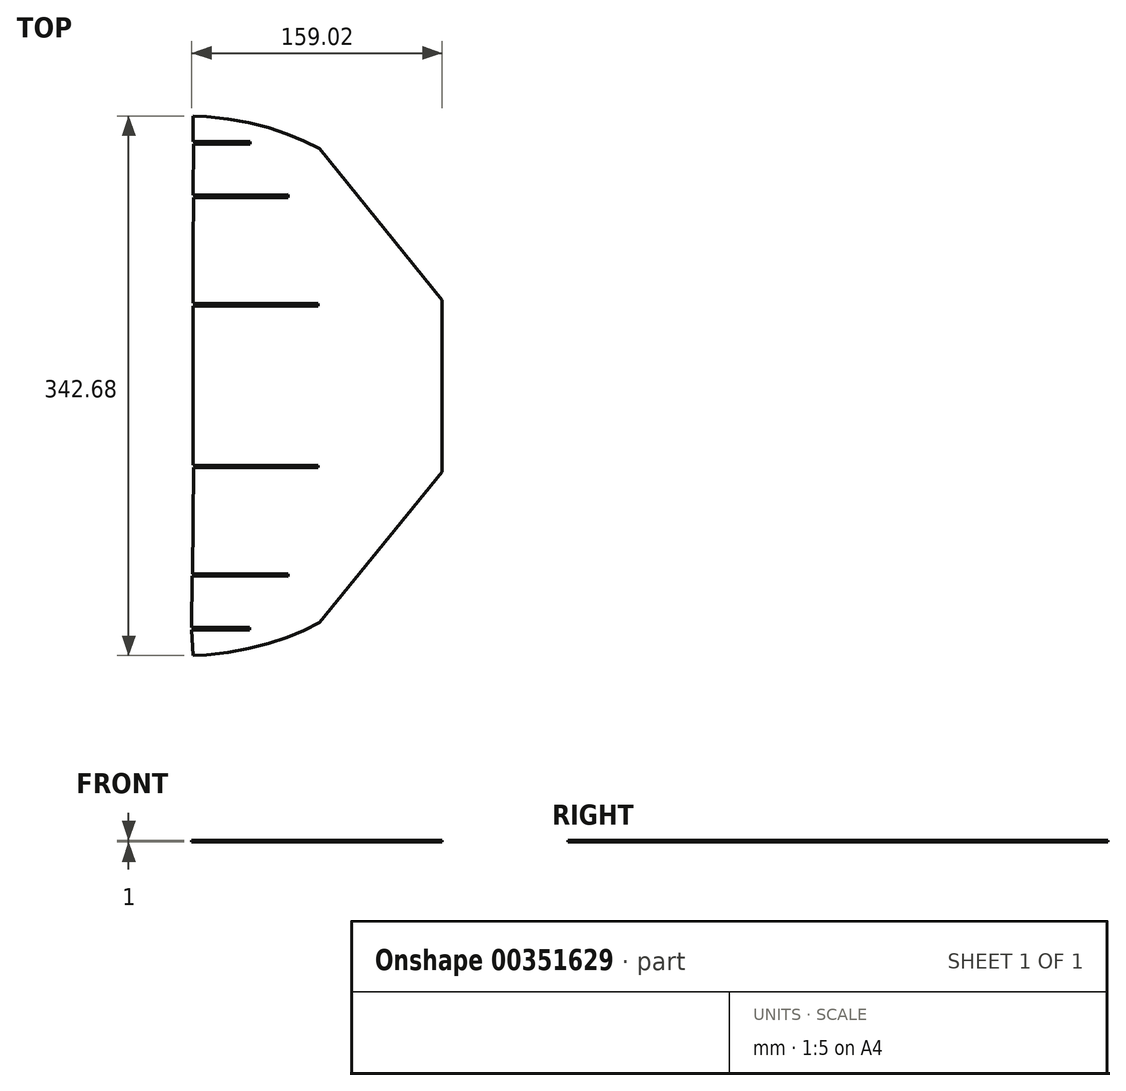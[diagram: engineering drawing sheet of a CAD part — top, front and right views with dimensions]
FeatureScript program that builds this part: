
annotation { "Feature Type Name" : "Feature", "Feature Type Description" : "" }
export const myFeature = defineFeature(function(context is Context, id is Id, definition is map)
    precondition{}
    {
        {
            var Q0;
            Q0=qCreatedBy(makeId("Top.planeOp"),FACE);
            var sketch = newSketch(context, id + "F0", { "sketchPlane" : qUnion([Q0])});
            skLineSegment(sketch, "E0", {"start": v(-243.07, 79.46) * mm, "end": v(-243.07, 43.03) * mm});
            skLineSegment(sketch, "E1", {"start": v(-243.07, 43.03) * mm, "end": v(-163.48, 42.74) * mm});
            skLineSegment(sketch, "E2", {"start": v(-163.48, 42.74) * mm, "end": v(-163.48, 41.46) * mm});
            skLineSegment(sketch, "E3", {"start": v(-163.48, 41.46) * mm, "end": v(-242.77, 41.46) * mm});
            skLineSegment(sketch, "E4", {"start": v(-242.77, 41.46) * mm, "end": v(-243.07, 10.85) * mm});
            skLineSegment(sketch, "E5", {"start": v(-243.07, 10.85) * mm, "end": v(-242.77, 4.68) * mm});
            skLineSegment(sketch, "E6", {"start": v(-242.77, 4.68) * mm, "end": v(-243.07, -25.94) * mm});
            skLineSegment(sketch, "E7", {"start": v(-243.07, -25.94) * mm, "end": v(-182.54, -26.22) * mm});
            skLineSegment(sketch, "E8", {"start": v(-182.54, -26.22) * mm, "end": v(-182.54, -27.51) * mm});
            skLineSegment(sketch, "E9", {"start": v(-182.54, -27.51) * mm, "end": v(-242.77, -27.51) * mm});
            skLineSegment(sketch, "E10", {"start": v(-242.77, -27.51) * mm, "end": v(-243.07, -60.24) * mm});
            skLineSegment(sketch, "E11", {"start": v(-243.07, -60.24) * mm, "end": v(-206.7, -60.53) * mm});
            skLineSegment(sketch, "E12", {"start": v(-206.7, -60.53) * mm, "end": v(-206.7, -61.82) * mm});
            skLineSegment(sketch, "E13", {"start": v(-206.7, -61.82) * mm, "end": v(-242.77, -61.82) * mm});
            skLineSegment(sketch, "E14", {"start": v(-242.77, -61.82) * mm, "end": v(-243.07, -77.95) * mm});
            skLineSegment(sketch, "E15", {"start": v(-243.07, -77.95) * mm, "end": v(-234.35, -77.61) * mm});
            skLineSegment(sketch, "E16", {"start": v(-234.35, -77.61) * mm, "end": v(-220.76, -76.07) * mm});
            skLineSegment(sketch, "E17", {"start": v(-220.76, -76.07) * mm, "end": v(-207.58, -73.65) * mm});
            skLineSegment(sketch, "E18", {"start": v(-207.58, -73.65) * mm, "end": v(-195.03, -70.42) * mm});
            skLineSegment(sketch, "E19", {"start": v(-195.03, -70.42) * mm, "end": v(-183.3, -66.5) * mm});
            skLineSegment(sketch, "E20", {"start": v(-183.3, -66.5) * mm, "end": v(-172.44, -62.03) * mm});
            skLineSegment(sketch, "E21", {"start": v(-172.44, -62.03) * mm, "end": v(-162.46, -57.15) * mm});
            skLineSegment(sketch, "E22", {"start": v(-243.07, 113.78) * mm, "end": v(-243.07, 79.46) * mm});
            skLineSegment(sketch, "E23", {"start": v(-242.77, 143.67) * mm, "end": v(-243.07, 113.76) * mm});
            skLineSegment(sketch, "E24", {"start": v(-243.07, 182.38) * mm, "end": v(-243.07, 145.95) * mm});
            skLineSegment(sketch, "E25", {"start": v(-243.07, 145.95) * mm, "end": v(-163.48, 145.67) * mm});
            skLineSegment(sketch, "E26", {"start": v(-162.46, 243.92) * mm, "end": v(-172.44, 248.8) * mm});
            skLineSegment(sketch, "E27", {"start": v(-172.44, 248.8) * mm, "end": v(-183.3, 253.28) * mm});
            skLineSegment(sketch, "E28", {"start": v(-183.3, 253.28) * mm, "end": v(-195.03, 257.2) * mm});
            skLineSegment(sketch, "E29", {"start": v(-195.03, 257.2) * mm, "end": v(-207.58, 260.42) * mm});
            skLineSegment(sketch, "E30", {"start": v(-207.58, 260.42) * mm, "end": v(-220.77, 262.85) * mm});
            skLineSegment(sketch, "E31", {"start": v(-220.77, 262.85) * mm, "end": v(-234.35, 264.38) * mm});
            skLineSegment(sketch, "E32", {"start": v(-234.35, 264.38) * mm, "end": v(-243.07, 264.72) * mm});
            skLineSegment(sketch, "E33", {"start": v(-243.07, 264.72) * mm, "end": v(-243.07, 248.53) * mm});
            skLineSegment(sketch, "E34", {"start": v(-243.07, 248.53) * mm, "end": v(-206.7, 248.24) * mm});
            skLineSegment(sketch, "E35", {"start": v(-206.7, 248.24) * mm, "end": v(-206.7, 246.95) * mm});
            skLineSegment(sketch, "E36", {"start": v(-206.7, 246.95) * mm, "end": v(-242.77, 246.95) * mm});
            skLineSegment(sketch, "E37", {"start": v(-242.77, 246.95) * mm, "end": v(-243.07, 214.93) * mm});
            skLineSegment(sketch, "E38", {"start": v(-243.07, 214.93) * mm, "end": v(-182.55, 214.63) * mm});
            skLineSegment(sketch, "E39", {"start": v(-182.55, 214.63) * mm, "end": v(-182.55, 213) * mm});
            skLineSegment(sketch, "E40", {"start": v(-182.55, 213) * mm, "end": v(-242.77, 213) * mm});
            skLineSegment(sketch, "E41", {"start": v(-242.77, 213) * mm, "end": v(-243.07, 182.38) * mm});
            skLineSegment(sketch, "E42", {"start": v(-163.85, 41.31) * mm, "end": v(-243.07, 41.33) * mm});
            skLineSegment(sketch, "E43", {"start": v(-243.07, 41.33) * mm, "end": v(-243.07, 42.83) * mm});
            skLineSegment(sketch, "E44", {"start": v(-243.07, 42.83) * mm, "end": v(-163.85, 42.81) * mm});
            skLineSegment(sketch, "E45", {"start": v(-163.85, 42.81) * mm, "end": v(-163.85, 41.31) * mm});
            skLineSegment(sketch, "E46", {"start": v(-84.88, 38.63) * mm, "end": v(-162.46, -57.15) * mm});
            skLineSegment(sketch, "E47", {"start": v(-162.46, 243.92) * mm, "end": v(-84.76, 147.77) * mm});
            skLineSegment(sketch, "E48", {"start": v(-84.76, 147.77) * mm, "end": v(-84.88, 38.63) * mm});
            skLineSegment(sketch, "E49", {"start": v(-163.7, 144.04) * mm, "end": v(-242.92, 144.05) * mm});
            skLineSegment(sketch, "E50", {"start": v(-242.92, 144.05) * mm, "end": v(-242.92, 145.55) * mm});
            skLineSegment(sketch, "E51", {"start": v(-242.92, 145.55) * mm, "end": v(-163.7, 145.54) * mm});
            skLineSegment(sketch, "E52", {"start": v(-163.7, 145.54) * mm, "end": v(-163.7, 144.04) * mm});
            skLineSegment(sketch, "E53", {"start": v(-243.07, 143.77) * mm, "end": v(-163.48, 143.77) * mm});
            skLineSegment(sketch, "E54", {"start": v(-182.92, 213.03) * mm, "end": v(-242.92, 213.04) * mm});
            skLineSegment(sketch, "E55", {"start": v(-242.92, 213.04) * mm, "end": v(-242.92, 214.54) * mm});
            skLineSegment(sketch, "E56", {"start": v(-242.92, 214.54) * mm, "end": v(-182.92, 214.53) * mm});
            skLineSegment(sketch, "E57", {"start": v(-182.92, 214.53) * mm, "end": v(-182.92, 213.03) * mm});
            skLineSegment(sketch, "E58", {"start": v(-182.52, -27.65) * mm, "end": v(-243.07, -27.64) * mm});
            skLineSegment(sketch, "E59", {"start": v(-243.07, -27.64) * mm, "end": v(-243.07, -26.14) * mm});
            skLineSegment(sketch, "E60", {"start": v(-243.07, -26.14) * mm, "end": v(-182.52, -26.15) * mm});
            skLineSegment(sketch, "E61", {"start": v(-182.52, -26.15) * mm, "end": v(-182.52, -27.65) * mm});
            skLineSegment(sketch, "E62", {"start": v(-207.2, -61.7) * mm, "end": v(-243.07, -61.68) * mm});
            skLineSegment(sketch, "E63", {"start": v(-243.07, -61.68) * mm, "end": v(-243.07, -60.18) * mm});
            skLineSegment(sketch, "E64", {"start": v(-243.07, -60.18) * mm, "end": v(-207.2, -60.2) * mm});
            skLineSegment(sketch, "E65", {"start": v(-207.2, -60.2) * mm, "end": v(-207.2, -61.7) * mm});
            skLineSegment(sketch, "E66", {"start": v(-206.67, 247.05) * mm, "end": v(-243.06, 247.05) * mm});
            skLineSegment(sketch, "E67", {"start": v(-243.06, 247.05) * mm, "end": v(-243.06, 248.55) * mm});
            skLineSegment(sketch, "E68", {"start": v(-243.06, 248.55) * mm, "end": v(-206.66, 248.55) * mm});
            skLineSegment(sketch, "E69", {"start": v(-206.66, 248.55) * mm, "end": v(-206.67, 247.05) * mm});
            skLineSegment(sketch, "E70", {"start": v(-79.3, 72.55) * mm, "end": v(-79.3, 36.12) * mm});
            skLineSegment(sketch, "E71", {"start": v(-79.3, 36.12) * mm, "end": v(0.28, 35.83) * mm});
            skLineSegment(sketch, "E72", {"start": v(0.28, 35.83) * mm, "end": v(0.28, 34.55) * mm});
            skLineSegment(sketch, "E73", {"start": v(0.28, 34.55) * mm, "end": v(-79, 34.55) * mm});
            skLineSegment(sketch, "E74", {"start": v(-79, 34.55) * mm, "end": v(-79.3, 3.94) * mm});
            skLineSegment(sketch, "E75", {"start": v(-79.3, 3.94) * mm, "end": v(-79, -2.23) * mm});
            skLineSegment(sketch, "E76", {"start": v(-79, -2.23) * mm, "end": v(-79.3, -32.84) * mm});
            skLineSegment(sketch, "E77", {"start": v(-79.3, -32.84) * mm, "end": v(-18.78, -33.13) * mm});
            skLineSegment(sketch, "E78", {"start": v(-18.78, -33.13) * mm, "end": v(-18.78, -34.42) * mm});
            skLineSegment(sketch, "E79", {"start": v(-18.78, -34.42) * mm, "end": v(-79, -34.42) * mm});
            skLineSegment(sketch, "E80", {"start": v(-79, -34.42) * mm, "end": v(-79.3, -67.15) * mm});
            skLineSegment(sketch, "E81", {"start": v(-79.3, -67.15) * mm, "end": v(-42.93, -67.44) * mm});
            skLineSegment(sketch, "E82", {"start": v(-42.93, -67.44) * mm, "end": v(-42.93, -68.73) * mm});
            skLineSegment(sketch, "E83", {"start": v(-42.93, -68.73) * mm, "end": v(-79, -68.73) * mm});
            skLineSegment(sketch, "E84", {"start": v(-79, -68.73) * mm, "end": v(-79.3, -84.86) * mm});
            skLineSegment(sketch, "E85", {"start": v(-79.3, -84.86) * mm, "end": v(-70.59, -84.52) * mm});
            skLineSegment(sketch, "E86", {"start": v(-70.59, -84.52) * mm, "end": v(-57, -82.98) * mm});
            skLineSegment(sketch, "E87", {"start": v(-57, -82.98) * mm, "end": v(-43.82, -80.56) * mm});
            skLineSegment(sketch, "E88", {"start": v(-43.82, -80.56) * mm, "end": v(-31.26, -77.33) * mm});
            skLineSegment(sketch, "E89", {"start": v(-31.26, -77.33) * mm, "end": v(-19.54, -73.4) * mm});
            skLineSegment(sketch, "E90", {"start": v(-19.54, -73.4) * mm, "end": v(-8.68, -68.94) * mm});
            skLineSegment(sketch, "E91", {"start": v(-8.68, -68.94) * mm, "end": v(1.3, -64.06) * mm});
            skLineSegment(sketch, "E92", {"start": v(-79.3, 106.87) * mm, "end": v(-79.3, 72.55) * mm});
            skLineSegment(sketch, "E93", {"start": v(-79, 136.76) * mm, "end": v(-79.3, 106.86) * mm});
            skLineSegment(sketch, "E94", {"start": v(-79.3, 175.47) * mm, "end": v(-79.3, 139.04) * mm});
            skLineSegment(sketch, "E95", {"start": v(-79.3, 139.04) * mm, "end": v(0.28, 138.76) * mm});
            skLineSegment(sketch, "E96", {"start": v(1.3, 237.02) * mm, "end": v(-8.68, 241.9) * mm});
            skLineSegment(sketch, "E97", {"start": v(-8.68, 241.9) * mm, "end": v(-19.54, 246.37) * mm});
            skLineSegment(sketch, "E98", {"start": v(-19.54, 246.37) * mm, "end": v(-31.26, 250.29) * mm});
            skLineSegment(sketch, "E99", {"start": v(-31.26, 250.29) * mm, "end": v(-43.82, 253.5) * mm});
            skLineSegment(sketch, "E100", {"start": v(-43.82, 253.5) * mm, "end": v(-57, 255.94) * mm});
            skLineSegment(sketch, "E101", {"start": v(-57, 255.94) * mm, "end": v(-70.59, 257.47) * mm});
            skLineSegment(sketch, "E102", {"start": v(-70.59, 257.47) * mm, "end": v(-79.3, 257.81) * mm});
            skLineSegment(sketch, "E103", {"start": v(-79.3, 257.81) * mm, "end": v(-79.3, 241.62) * mm});
            skLineSegment(sketch, "E104", {"start": v(-79.3, 241.62) * mm, "end": v(-42.93, 241.33) * mm});
            skLineSegment(sketch, "E105", {"start": v(-42.93, 241.33) * mm, "end": v(-42.93, 240.04) * mm});
            skLineSegment(sketch, "E106", {"start": v(-42.93, 240.04) * mm, "end": v(-79, 240.04) * mm});
            skLineSegment(sketch, "E107", {"start": v(-79, 240.04) * mm, "end": v(-79.3, 208.02) * mm});
            skLineSegment(sketch, "E108", {"start": v(-79.3, 208.02) * mm, "end": v(-18.79, 207.73) * mm});
            skLineSegment(sketch, "E109", {"start": v(-18.79, 207.73) * mm, "end": v(-18.79, 206.09) * mm});
            skLineSegment(sketch, "E110", {"start": v(-18.79, 206.09) * mm, "end": v(-79, 206.09) * mm});
            skLineSegment(sketch, "E111", {"start": v(-79, 206.09) * mm, "end": v(-79.3, 175.47) * mm});
            skLineSegment(sketch, "E112", {"start": v(-0.09, 34.4) * mm, "end": v(-79.3, 34.42) * mm});
            skLineSegment(sketch, "E113", {"start": v(-79.3, 34.42) * mm, "end": v(-79.3, 35.92) * mm});
            skLineSegment(sketch, "E114", {"start": v(-79.3, 35.92) * mm, "end": v(-0.09, 35.9) * mm});
            skLineSegment(sketch, "E115", {"start": v(-0.09, 35.9) * mm, "end": v(-0.09, 34.4) * mm});
            skLineSegment(sketch, "E116", {"start": v(78.88, 31.72) * mm, "end": v(1.3, -64.06) * mm});
            skLineSegment(sketch, "E117", {"start": v(1.3, 237.02) * mm, "end": v(79, 140.86) * mm});
            skLineSegment(sketch, "E118", {"start": v(79, 140.86) * mm, "end": v(78.88, 31.72) * mm});
            skLineSegment(sketch, "E119", {"start": v(0.06, 137.13) * mm, "end": v(-79.15, 137.14) * mm});
            skLineSegment(sketch, "E120", {"start": v(-79.15, 137.14) * mm, "end": v(-79.15, 138.64) * mm});
            skLineSegment(sketch, "E121", {"start": v(-79.15, 138.64) * mm, "end": v(0.06, 138.63) * mm});
            skLineSegment(sketch, "E122", {"start": v(0.06, 138.63) * mm, "end": v(0.06, 137.13) * mm});
            skLineSegment(sketch, "E123", {"start": v(-79.3, 136.86) * mm, "end": v(0.28, 136.86) * mm});
            skLineSegment(sketch, "E124", {"start": v(-19.16, 206.12) * mm, "end": v(-79.15, 206.14) * mm});
            skLineSegment(sketch, "E125", {"start": v(-79.15, 206.14) * mm, "end": v(-79.15, 207.64) * mm});
            skLineSegment(sketch, "E126", {"start": v(-79.15, 207.64) * mm, "end": v(-19.16, 207.62) * mm});
            skLineSegment(sketch, "E127", {"start": v(-19.16, 207.62) * mm, "end": v(-19.16, 206.12) * mm});
            skLineSegment(sketch, "E128", {"start": v(-18.75, -34.56) * mm, "end": v(-79.3, -34.55) * mm});
            skLineSegment(sketch, "E129", {"start": v(-79.3, -34.55) * mm, "end": v(-79.3, -33.05) * mm});
            skLineSegment(sketch, "E130", {"start": v(-79.3, -33.05) * mm, "end": v(-18.75, -33.06) * mm});
            skLineSegment(sketch, "E131", {"start": v(-18.75, -33.06) * mm, "end": v(-18.75, -34.56) * mm});
            skLineSegment(sketch, "E132", {"start": v(-43.43, -68.6) * mm, "end": v(-79.3, -68.6) * mm});
            skLineSegment(sketch, "E133", {"start": v(-79.3, -68.6) * mm, "end": v(-79.3, -67.1) * mm});
            skLineSegment(sketch, "E134", {"start": v(-79.3, -67.1) * mm, "end": v(-43.43, -67.1) * mm});
            skLineSegment(sketch, "E135", {"start": v(-43.43, -67.1) * mm, "end": v(-43.43, -68.6) * mm});
            skLineSegment(sketch, "E136", {"start": v(-42.9, 240.14) * mm, "end": v(-79.3, 240.14) * mm});
            skLineSegment(sketch, "E137", {"start": v(-79.3, 240.14) * mm, "end": v(-79.3, 241.64) * mm});
            skLineSegment(sketch, "E138", {"start": v(-79.3, 241.64) * mm, "end": v(-42.9, 241.64) * mm});
            skLineSegment(sketch, "E139", {"start": v(-42.9, 241.64) * mm, "end": v(-42.9, 240.14) * mm});
            skLineSegment(sketch, "E140", {"start": v(84.76, 65.53) * mm, "end": v(84.76, 29.1) * mm});
            skLineSegment(sketch, "E141", {"start": v(84.76, 29.1) * mm, "end": v(164.34, 28.82) * mm});
            skLineSegment(sketch, "E142", {"start": v(164.34, 28.82) * mm, "end": v(164.34, 27.54) * mm});
            skLineSegment(sketch, "E143", {"start": v(164.34, 27.54) * mm, "end": v(85.06, 27.54) * mm});
            skLineSegment(sketch, "E144", {"start": v(84.4, -40.06) * mm, "end": v(145.28, -40.15) * mm});
            skLineSegment(sketch, "E145", {"start": v(145.28, -40.15) * mm, "end": v(145.28, -41.44) * mm});
            skLineSegment(sketch, "E146", {"start": v(145.28, -41.44) * mm, "end": v(84.38, -41.51) * mm});
            skLineSegment(sketch, "E147", {"start": v(84.38, -41.51) * mm, "end": v(84.06, -74.07) * mm});
            skLineSegment(sketch, "E148", {"start": v(120.63, -75.62) * mm, "end": v(84.05, -75.74) * mm});
            skLineSegment(sketch, "E149", {"start": v(84.05, -75.74) * mm, "end": v(84.76, -91.88) * mm});
            skLineSegment(sketch, "E150", {"start": v(84.76, -91.88) * mm, "end": v(93.47, -91.54) * mm});
            skLineSegment(sketch, "E151", {"start": v(93.47, -91.54) * mm, "end": v(107.07, -90) * mm});
            skLineSegment(sketch, "E152", {"start": v(107.07, -90) * mm, "end": v(120.24, -87.58) * mm});
            skLineSegment(sketch, "E153", {"start": v(120.24, -87.58) * mm, "end": v(132.8, -84.35) * mm});
            skLineSegment(sketch, "E154", {"start": v(132.8, -84.35) * mm, "end": v(144.52, -80.42) * mm});
            skLineSegment(sketch, "E155", {"start": v(144.52, -80.42) * mm, "end": v(155.38, -75.96) * mm});
            skLineSegment(sketch, "E156", {"start": v(155.38, -75.96) * mm, "end": v(165.37, -71.08) * mm});
            skLineSegment(sketch, "E157", {"start": v(84.76, 99.85) * mm, "end": v(84.76, 65.53) * mm});
            skLineSegment(sketch, "E158", {"start": v(84.91, 130.13) * mm, "end": v(84.76, 99.84) * mm});
            skLineSegment(sketch, "E159", {"start": v(84.76, 168.45) * mm, "end": v(84.76, 132.03) * mm});
            skLineSegment(sketch, "E160", {"start": v(84.76, 132.03) * mm, "end": v(164.13, 131.61) * mm});
            skLineSegment(sketch, "E161", {"start": v(165.37, 230) * mm, "end": v(155.38, 234.88) * mm});
            skLineSegment(sketch, "E162", {"start": v(155.38, 234.88) * mm, "end": v(144.52, 239.36) * mm});
            skLineSegment(sketch, "E163", {"start": v(144.52, 239.36) * mm, "end": v(132.8, 243.27) * mm});
            skLineSegment(sketch, "E164", {"start": v(132.8, 243.27) * mm, "end": v(120.24, 246.5) * mm});
            skLineSegment(sketch, "E165", {"start": v(120.24, 246.5) * mm, "end": v(107.06, 248.92) * mm});
            skLineSegment(sketch, "E166", {"start": v(107.06, 248.92) * mm, "end": v(93.47, 250.45) * mm});
            skLineSegment(sketch, "E167", {"start": v(93.47, 250.45) * mm, "end": v(84.76, 250.8) * mm});
            skLineSegment(sketch, "E168", {"start": v(84.76, 250.8) * mm, "end": v(84.76, 234.6) * mm});
            skLineSegment(sketch, "E169", {"start": v(84.76, 234.6) * mm, "end": v(121.13, 234.32) * mm});
            skLineSegment(sketch, "E170", {"start": v(121.13, 234.32) * mm, "end": v(121.13, 233.03) * mm});
            skLineSegment(sketch, "E171", {"start": v(121.13, 233.03) * mm, "end": v(85.06, 233.03) * mm});
            skLineSegment(sketch, "E172", {"start": v(85.06, 233.03) * mm, "end": v(84.91, 200.62) * mm});
            skLineSegment(sketch, "E173", {"start": v(84.91, 200.62) * mm, "end": v(145.27, 200.7) * mm});
            skLineSegment(sketch, "E174", {"start": v(145.27, 200.7) * mm, "end": v(145.27, 199.07) * mm});
            skLineSegment(sketch, "E175", {"start": v(145.27, 199.07) * mm, "end": v(85.06, 199.07) * mm});
            skLineSegment(sketch, "E176", {"start": v(85.06, 199.07) * mm, "end": v(84.76, 168.45) * mm});
            skLineSegment(sketch, "E177", {"start": v(163.98, 27.39) * mm, "end": v(84.76, 27.4) * mm});
            skLineSegment(sketch, "E178", {"start": v(84.76, 27.4) * mm, "end": v(84.76, 28.9) * mm});
            skLineSegment(sketch, "E179", {"start": v(84.76, 28.9) * mm, "end": v(163.98, 28.89) * mm});
            skLineSegment(sketch, "E180", {"start": v(163.98, 28.89) * mm, "end": v(163.98, 27.39) * mm});
            skLineSegment(sketch, "E181", {"start": v(242.94, 24.7) * mm, "end": v(165.37, -71.08) * mm});
            skLineSegment(sketch, "E182", {"start": v(165.37, 230) * mm, "end": v(243.07, 133.84) * mm});
            skLineSegment(sketch, "E183", {"start": v(243.07, 133.84) * mm, "end": v(242.94, 24.7) * mm});
            skLineSegment(sketch, "E184", {"start": v(164.13, 130.11) * mm, "end": v(84.91, 130.13) * mm});
            skLineSegment(sketch, "E185", {"start": v(164.13, 131.61) * mm, "end": v(164.13, 130.11) * mm});
            skLineSegment(sketch, "E186", {"start": v(144.9, 199.1) * mm, "end": v(84.91, 199.12) * mm});
            skLineSegment(sketch, "E187", {"start": v(84.91, 199.12) * mm, "end": v(84.91, 200.62) * mm});
            skLineSegment(sketch, "E188", {"start": v(84.91, 200.62) * mm, "end": v(144.9, 200.6) * mm});
            skLineSegment(sketch, "E189", {"start": v(144.9, 200.6) * mm, "end": v(144.9, 199.1) * mm});
            skLineSegment(sketch, "E190", {"start": v(145.31, -41.57) * mm, "end": v(84.38, -41.51) * mm});
            skLineSegment(sketch, "E191", {"start": v(84.4, -40.06) * mm, "end": v(145.31, -40.07) * mm});
            skLineSegment(sketch, "E192", {"start": v(145.31, -40.07) * mm, "end": v(145.31, -41.57) * mm});
            skLineSegment(sketch, "E193", {"start": v(84.06, -74.07) * mm, "end": v(120.63, -74.12) * mm});
            skLineSegment(sketch, "E194", {"start": v(120.63, -74.12) * mm, "end": v(120.63, -75.62) * mm});
            skLineSegment(sketch, "E195", {"start": v(121.16, 233.12) * mm, "end": v(84.77, 233.13) * mm});
            skLineSegment(sketch, "E196", {"start": v(84.77, 233.13) * mm, "end": v(84.77, 234.63) * mm});
            skLineSegment(sketch, "E197", {"start": v(84.77, 234.63) * mm, "end": v(121.16, 234.62) * mm});
            skLineSegment(sketch, "E198", {"start": v(121.16, 234.62) * mm, "end": v(121.16, 233.12) * mm});
            skLineSegment(sketch, "E199", {"start": v(-57.5, -264.72) * mm, "end": v(-21.07, -264.72) * mm});
            skLineSegment(sketch, "E200", {"start": v(-21.07, -264.72) * mm, "end": v(-20.78, -185.14) * mm});
            skLineSegment(sketch, "E201", {"start": v(-20.78, -185.14) * mm, "end": v(-19.5, -185.14) * mm});
            skLineSegment(sketch, "E202", {"start": v(-19.5, -185.14) * mm, "end": v(-19.5, -264.42) * mm});
            skLineSegment(sketch, "E203", {"start": v(-19.5, -264.42) * mm, "end": v(11.1, -264.72) * mm});
            skLineSegment(sketch, "E204", {"start": v(11.1, -264.72) * mm, "end": v(17.28, -264.42) * mm});
            skLineSegment(sketch, "E205", {"start": v(17.28, -264.42) * mm, "end": v(47.9, -264.72) * mm});
            skLineSegment(sketch, "E206", {"start": v(47.9, -264.72) * mm, "end": v(48.18, -204.2) * mm});
            skLineSegment(sketch, "E207", {"start": v(48.18, -204.2) * mm, "end": v(49.47, -204.2) * mm});
            skLineSegment(sketch, "E208", {"start": v(49.47, -204.2) * mm, "end": v(49.47, -264.42) * mm});
            skLineSegment(sketch, "E209", {"start": v(49.47, -264.42) * mm, "end": v(82.2, -264.72) * mm});
            skLineSegment(sketch, "E210", {"start": v(82.2, -264.72) * mm, "end": v(82.49, -228.35) * mm});
            skLineSegment(sketch, "E211", {"start": v(82.49, -228.35) * mm, "end": v(83.77, -228.35) * mm});
            skLineSegment(sketch, "E212", {"start": v(83.77, -228.35) * mm, "end": v(83.77, -264.42) * mm});
            skLineSegment(sketch, "E213", {"start": v(83.77, -264.42) * mm, "end": v(99.91, -264.72) * mm});
            skLineSegment(sketch, "E214", {"start": v(99.91, -264.72) * mm, "end": v(99.57, -256) * mm});
            skLineSegment(sketch, "E215", {"start": v(99.57, -256) * mm, "end": v(98.03, -242.41) * mm});
            skLineSegment(sketch, "E216", {"start": v(98.03, -242.41) * mm, "end": v(95.61, -229.24) * mm});
            skLineSegment(sketch, "E217", {"start": v(95.61, -229.24) * mm, "end": v(92.38, -216.68) * mm});
            skLineSegment(sketch, "E218", {"start": v(92.38, -216.68) * mm, "end": v(88.46, -204.96) * mm});
            skLineSegment(sketch, "E219", {"start": v(88.46, -204.96) * mm, "end": v(83.99, -194.1) * mm});
            skLineSegment(sketch, "E220", {"start": v(83.99, -194.1) * mm, "end": v(79.11, -184.11) * mm});
            skLineSegment(sketch, "E221", {"start": v(-91.82, -264.72) * mm, "end": v(-57.5, -264.72) * mm});
            skLineSegment(sketch, "E222", {"start": v(-121.71, -264.42) * mm, "end": v(-91.8, -264.72) * mm});
            skLineSegment(sketch, "E223", {"start": v(-160.42, -264.72) * mm, "end": v(-124, -264.72) * mm});
            skLineSegment(sketch, "E224", {"start": v(-124, -264.72) * mm, "end": v(-123.71, -185.14) * mm});
            skLineSegment(sketch, "E225", {"start": v(-221.97, -184.11) * mm, "end": v(-226.84, -194.1) * mm});
            skLineSegment(sketch, "E226", {"start": v(-226.84, -194.1) * mm, "end": v(-231.32, -204.96) * mm});
            skLineSegment(sketch, "E227", {"start": v(-231.32, -204.96) * mm, "end": v(-235.24, -216.68) * mm});
            skLineSegment(sketch, "E228", {"start": v(-235.24, -216.68) * mm, "end": v(-238.46, -229.24) * mm});
            skLineSegment(sketch, "E229", {"start": v(-238.46, -229.24) * mm, "end": v(-240.89, -242.42) * mm});
            skLineSegment(sketch, "E230", {"start": v(-240.89, -242.42) * mm, "end": v(-242.42, -256) * mm});
            skLineSegment(sketch, "E231", {"start": v(-242.42, -256) * mm, "end": v(-242.77, -264.72) * mm});
            skLineSegment(sketch, "E232", {"start": v(-242.77, -264.72) * mm, "end": v(-226.57, -264.72) * mm});
            skLineSegment(sketch, "E233", {"start": v(-226.57, -264.72) * mm, "end": v(-226.29, -228.35) * mm});
            skLineSegment(sketch, "E234", {"start": v(-226.29, -228.35) * mm, "end": v(-225, -228.35) * mm});
            skLineSegment(sketch, "E235", {"start": v(-225, -228.35) * mm, "end": v(-225, -264.42) * mm});
            skLineSegment(sketch, "E236", {"start": v(-225, -264.42) * mm, "end": v(-192.97, -264.72) * mm});
            skLineSegment(sketch, "E237", {"start": v(-192.97, -264.72) * mm, "end": v(-192.68, -204.2) * mm});
            skLineSegment(sketch, "E238", {"start": v(-192.68, -204.2) * mm, "end": v(-191.04, -204.2) * mm});
            skLineSegment(sketch, "E239", {"start": v(-191.04, -204.2) * mm, "end": v(-191.04, -264.42) * mm});
            skLineSegment(sketch, "E240", {"start": v(-191.04, -264.42) * mm, "end": v(-160.42, -264.72) * mm});
            skLineSegment(sketch, "E241", {"start": v(-19.35, -185.5) * mm, "end": v(-19.37, -264.72) * mm});
            skLineSegment(sketch, "E242", {"start": v(-19.37, -264.72) * mm, "end": v(-20.87, -264.72) * mm});
            skLineSegment(sketch, "E243", {"start": v(-20.87, -264.72) * mm, "end": v(-20.85, -185.5) * mm});
            skLineSegment(sketch, "E244", {"start": v(-20.85, -185.5) * mm, "end": v(-19.35, -185.5) * mm});
            skLineSegment(sketch, "E245", {"start": v(-16.67, -106.54) * mm, "end": v(79.11, -184.11) * mm});
            skLineSegment(sketch, "E246", {"start": v(-221.97, -184.11) * mm, "end": v(-125.8, -106.42) * mm});
            skLineSegment(sketch, "E247", {"start": v(-125.8, -106.42) * mm, "end": v(-16.67, -106.54) * mm});
            skLineSegment(sketch, "E248", {"start": v(-122.08, -185.36) * mm, "end": v(-122.1, -264.57) * mm});
            skLineSegment(sketch, "E249", {"start": v(-122.1, -264.57) * mm, "end": v(-123.6, -264.57) * mm});
            skLineSegment(sketch, "E250", {"start": v(-123.6, -264.57) * mm, "end": v(-123.58, -185.36) * mm});
            skLineSegment(sketch, "E251", {"start": v(-123.58, -185.36) * mm, "end": v(-122.08, -185.36) * mm});
            skLineSegment(sketch, "E252", {"start": v(-121.82, -264.72) * mm, "end": v(-121.82, -185.14) * mm});
            skLineSegment(sketch, "E253", {"start": v(-191.08, -204.58) * mm, "end": v(-191.09, -264.57) * mm});
            skLineSegment(sketch, "E254", {"start": v(-191.09, -264.57) * mm, "end": v(-192.59, -264.57) * mm});
            skLineSegment(sketch, "E255", {"start": v(-192.59, -264.57) * mm, "end": v(-192.58, -204.58) * mm});
            skLineSegment(sketch, "E256", {"start": v(-192.58, -204.58) * mm, "end": v(-191.08, -204.58) * mm});
            skLineSegment(sketch, "E257", {"start": v(49.6, -204.17) * mm, "end": v(49.6, -264.72) * mm});
            skLineSegment(sketch, "E258", {"start": v(49.6, -264.72) * mm, "end": v(48.1, -264.72) * mm});
            skLineSegment(sketch, "E259", {"start": v(48.1, -264.72) * mm, "end": v(48.1, -204.17) * mm});
            skLineSegment(sketch, "E260", {"start": v(48.1, -204.17) * mm, "end": v(49.6, -204.17) * mm});
            skLineSegment(sketch, "E261", {"start": v(83.65, -228.85) * mm, "end": v(83.64, -264.72) * mm});
            skLineSegment(sketch, "E262", {"start": v(83.64, -264.72) * mm, "end": v(82.14, -264.72) * mm});
            skLineSegment(sketch, "E263", {"start": v(82.14, -264.72) * mm, "end": v(82.15, -228.85) * mm});
            skLineSegment(sketch, "E264", {"start": v(82.15, -228.85) * mm, "end": v(83.65, -228.85) * mm});
            skLineSegment(sketch, "E265", {"start": v(-225.09, -228.32) * mm, "end": v(-225.1, -264.71) * mm});
            skLineSegment(sketch, "E266", {"start": v(-225.1, -264.71) * mm, "end": v(-226.6, -264.71) * mm});
            skLineSegment(sketch, "E267", {"start": v(-226.6, -264.71) * mm, "end": v(-226.59, -228.32) * mm});
            skLineSegment(sketch, "E268", {"start": v(-226.59, -228.32) * mm, "end": v(-225.09, -228.32) * mm});
            skLineSegment(sketch, "E269", {"start": v(85.06, 27.54) * mm, "end": v(84.4, -40.06) * mm});
            skSolve(sketch);
        }
        {
            var Q0;
            {var subQ23=sQuery(id+"F0.wireOp",EDGE,"E140");Q0=makeQuery(id+"F0.imprint","IMPRINT",FACE,{"disambiguationData":[TD([[makeQuery(id+"F0.imprint","IMPRINT",EDGE,{"derivedFrom":subQ23}),1.0]])]});}
            extrude(context, id + "F1", {"entities" : qUnion([Q0]), "depth" : 1 * mm});
        }
    });
